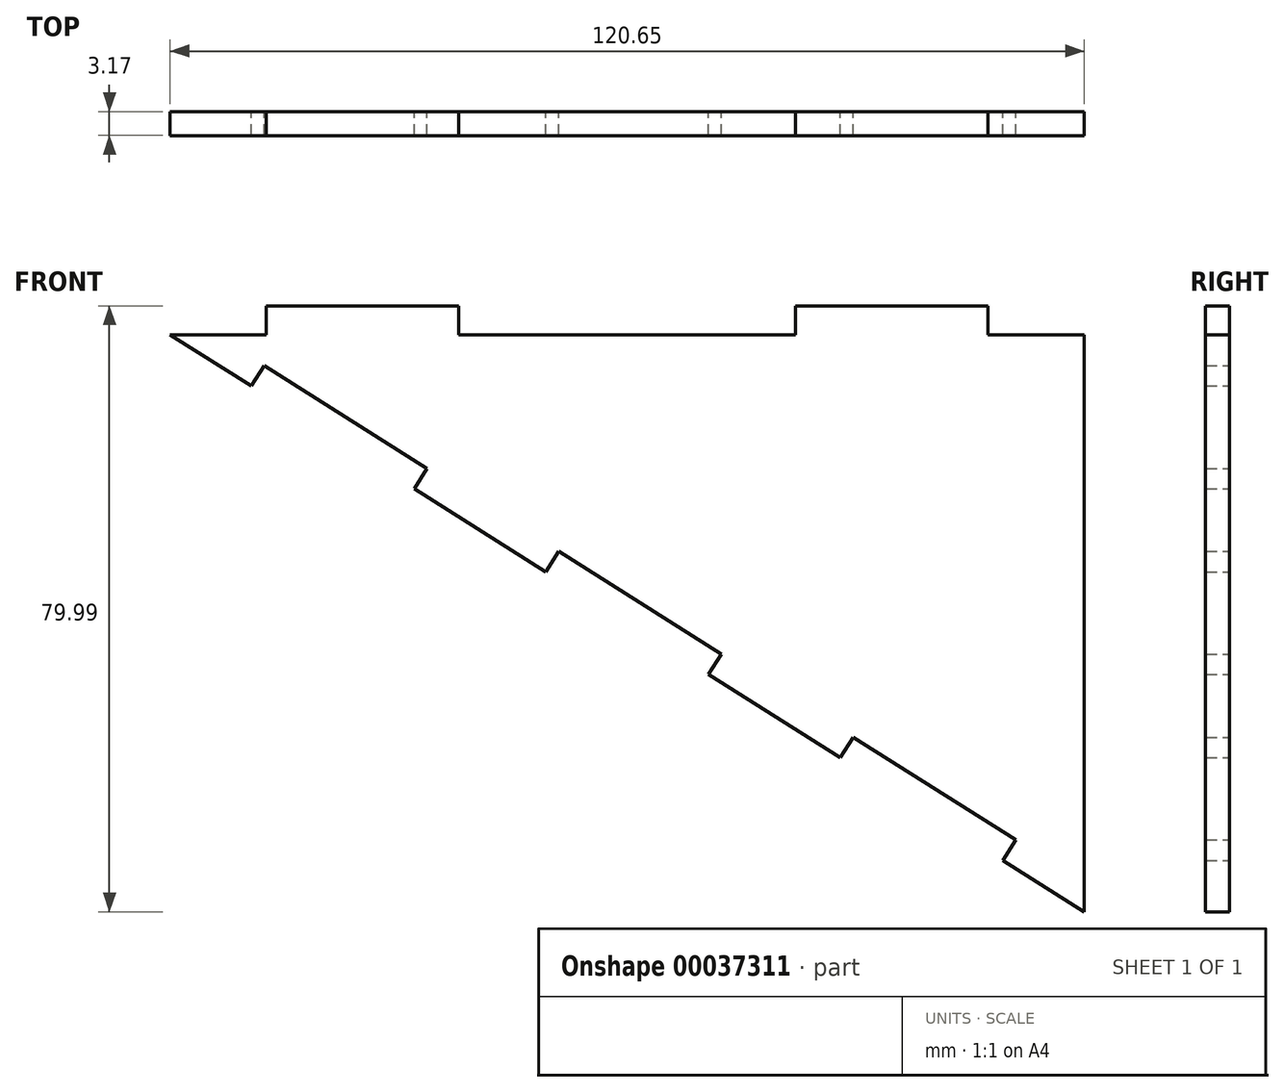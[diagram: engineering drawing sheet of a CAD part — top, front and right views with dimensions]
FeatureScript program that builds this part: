
annotation { "Feature Type Name" : "Feature", "Feature Type Description" : "" }
export const myFeature = defineFeature(function(context is Context, id is Id, definition is map)
    precondition{}
    {
        {
            var Q0;
            Q0=qCreatedBy(makeId("Front.planeOp"),FACE);
            var sketch = newSketch(context, id + "F0", { "sketchPlane" : qUnion([Q0])});
            skLineSegment(sketch, "E0", {"start": v(-62.93, 0) * mm, "end": v(57.72, 0) * mm});
            skLineSegment(sketch, "E1", {"start": v(57.72, 0) * mm, "end": v(57.72, -76.2) * mm});
            skLineSegment(sketch, "E2", {"start": v(-62.93, 0) * mm, "end": v(57.72, -76.2) * mm});
            skLineSegment(sketch, "E3", {"start": v(45.02, 0) * mm, "end": v(45.02, 3.79) * mm});
            skLineSegment(sketch, "E4", {"start": v(45.02, 3.79) * mm, "end": v(19.62, 3.79) * mm});
            skLineSegment(sketch, "E5", {"start": v(19.62, 3.79) * mm, "end": v(19.62, 0) * mm});
            skLineSegment(sketch, "E6", {"start": v(-50.23, 0) * mm, "end": v(-50.23, 3.79) * mm});
            skLineSegment(sketch, "E7", {"start": v(-50.23, 3.79) * mm, "end": v(-24.83, 3.79) * mm});
            skLineSegment(sketch, "E8", {"start": v(-24.83, 3.79) * mm, "end": v(-24.83, 0) * mm});
            skLineSegment(sketch, "E9", {"start": v(46.98, -69.42) * mm, "end": v(48.68, -66.73) * mm});
            skLineSegment(sketch, "E10", {"start": v(48.68, -66.73) * mm, "end": v(27.2, -53.17) * mm});
            skLineSegment(sketch, "E11", {"start": v(27.2, -53.17) * mm, "end": v(25.5, -55.85) * mm});
            skLineSegment(sketch, "E12", {"start": v(-52.2, -6.78) * mm, "end": v(-50.5, -4.1) * mm});
            skLineSegment(sketch, "E13", {"start": v(-50.5, -4.1) * mm, "end": v(-29.02, -17.66) * mm});
            skLineSegment(sketch, "E14", {"start": v(-29.02, -17.66) * mm, "end": v(-30.72, -20.35) * mm});
            skLineSegment(sketch, "E15", {"start": v(27.2, -53.17) * mm, "end": v(-29.02, -17.66) * mm, "construction": true});
            skLineSegment(sketch, "E16", {"start": v(-0.9, -35.42) * mm, "end": v(-2.6, -38.1) * mm, "construction": true});
            skLineSegment(sketch, "E17", {"start": v(8.13, -44.88) * mm, "end": v(9.83, -42.2) * mm});
            skLineSegment(sketch, "E18", {"start": v(9.83, -42.2) * mm, "end": v(-0.9, -35.42) * mm});
            skLineSegment(sketch, "E19", {"start": v(-13.34, -31.32) * mm, "end": v(-11.65, -28.63) * mm});
            skLineSegment(sketch, "E20", {"start": v(-11.65, -28.63) * mm, "end": v(-0.9, -35.42) * mm});
            skSolve(sketch);
        }
        {
            var Q0;
            {var subQ1=sQuery(id+"F0.wireOp",EDGE,"E3");Q0=makeQuery(id+"F0.imprint","IMPRINT",FACE,{"disambiguationData":[TD([[makeQuery(id+"F0.imprint","IMPRINT",EDGE,{"derivedFrom":subQ1}),1.0]])]});}
            var Q1;
            {var subQ1=sQuery(id+"F0.wireOp",EDGE,"E1");Q1=makeQuery(id+"F0.imprint","IMPRINT",FACE,{"disambiguationData":[TD([[makeQuery(id+"F0.imprint","IMPRINT",EDGE,{"derivedFrom":subQ1}),-1.0]])]});}
            var Q2;
            {var subQ1=sQuery(id+"F0.wireOp",EDGE,"E6");Q2=makeQuery(id+"F0.imprint","IMPRINT",FACE,{"disambiguationData":[TD([[makeQuery(id+"F0.imprint","IMPRINT",EDGE,{"derivedFrom":subQ1}),-1.0]])]});}
            extrude(context, id + "F1", {"entities" : qUnion([Q0, Q1, Q2]), "depth" : 3.17 * mm});
        }
    });
